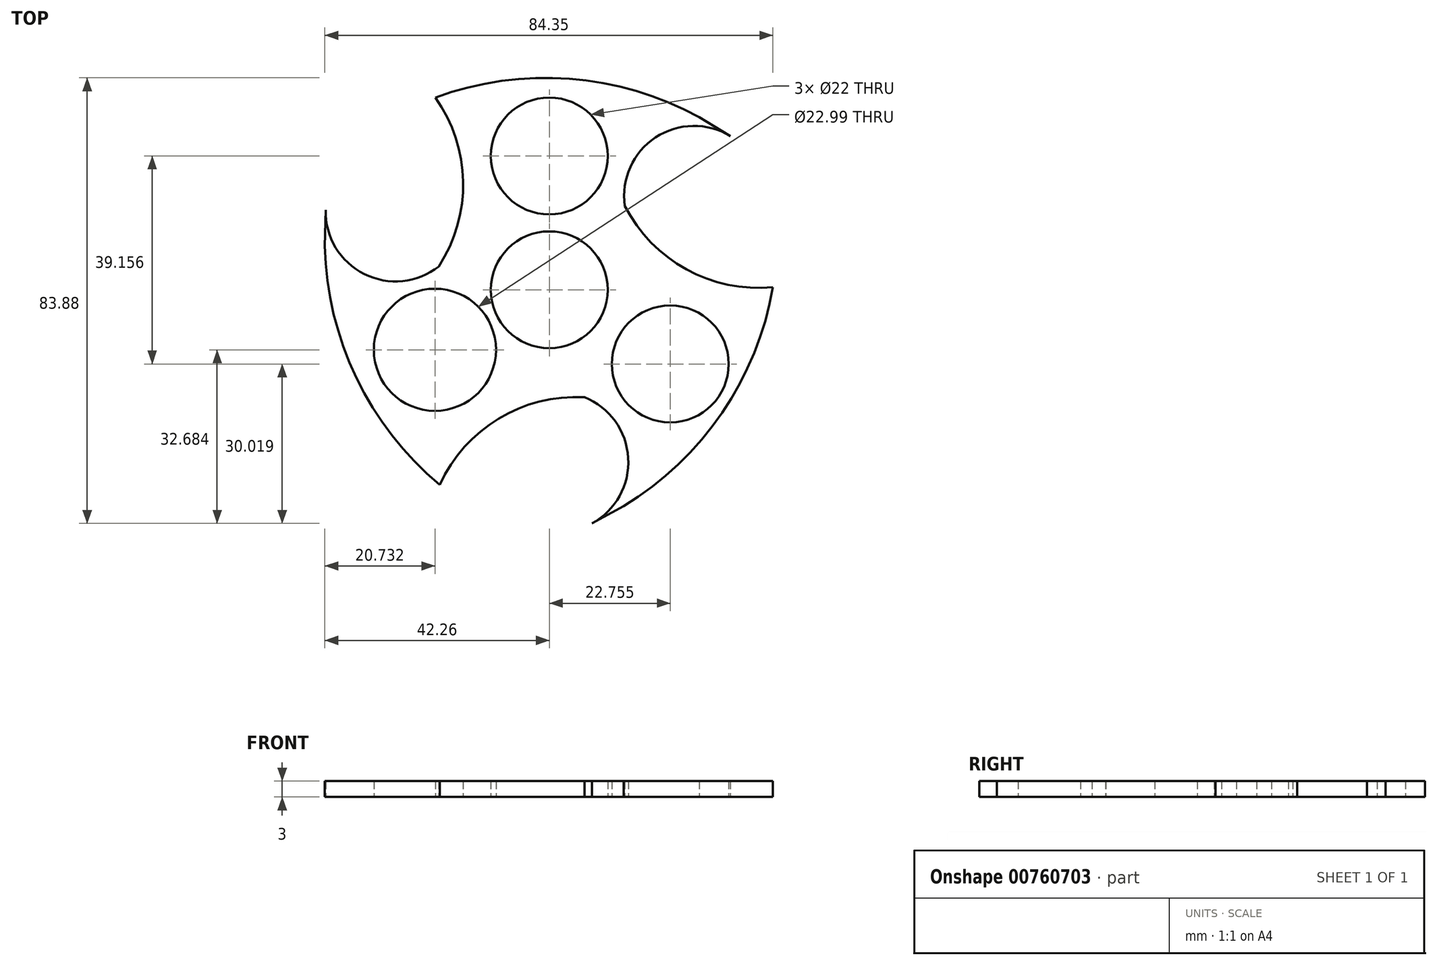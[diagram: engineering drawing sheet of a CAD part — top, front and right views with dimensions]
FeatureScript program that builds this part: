
annotation { "Feature Type Name" : "Feature", "Feature Type Description" : "" }
export const myFeature = defineFeature(function(context is Context, id is Id, definition is map)
    precondition{}
    {
        {
            var Q0;
            Q0=qCreatedBy(makeId("Top.planeOp"),FACE);
            var sketch = newSketch(context, id + "F0", { "sketchPlane" : qUnion([Q0])});
            skArc(sketch, "E0", {"start": v(28.24, 32.49) * mm, "mid": v(3.79, 39.73) * mm, "end": v(-21.47, 36.2) * mm});
            skArc(sketch, "E1", {"start": v(34.07, 28.95) * mm, "mid": v(19.98, 28.68) * mm, "end": v(14.21, 15.82) * mm});
            skArc(sketch, "E2", {"start": v(-20.8, 4.4) * mm, "mid": v(-16.22, 20.4) * mm, "end": v(-21.47, 36.2) * mm});
            skLineSegment(sketch, "E3", {"start": v(28.24, 32.49) * mm, "end": v(34.07, 28.95) * mm});
            skArc(sketch, "E4.1.5", {"start": v(9.53, 5.5) * mm, "mid": v(0, 11) * mm, "end": v(-9.53, 5.5) * mm});
            skArc(sketch, "E5.2.12", {"start": v(0, -11) * mm, "mid": v(9.53, -5.5) * mm, "end": v(9.53, 5.5) * mm});
            skCircle(sketch, "E6", {"center": v(0, 25.2) * mm, "radius": 11 * mm});
            skLineSegment(sketch, "E7.1.2", {"start": v(-42.26, 8.21) * mm, "end": v(-42.1, 15.04) * mm});
            skArc(sketch, "E7.1.4", {"start": v(6.6, -20.22) * mm, "mid": v(-9.56, -24.25) * mm, "end": v(-20.62, -36.7) * mm});
            skArc(sketch, "E7.1.5", {"start": v(-42.1, 15.04) * mm, "mid": v(-34.83, 2.97) * mm, "end": v(-20.8, 4.4) * mm});
            skCircle(sketch, "E7.1.6", {"center": v(-21.53, -11.3) * mm, "radius": 11.5 * mm});
            skArc(sketch, "E7.1.7", {"start": v(-42.26, 8.21) * mm, "mid": v(-36.3, -16.59) * mm, "end": v(-20.62, -36.7) * mm});
            skLineSegment(sketch, "E7.2.2", {"start": v(14.02, -40.7) * mm, "end": v(8.03, -43.98) * mm});
            skArc(sketch, "E7.2.3", {"start": v(-9.53, 5.5) * mm, "mid": v(-9.53, -5.5) * mm, "end": v(0, -11) * mm});
            skArc(sketch, "E7.2.4", {"start": v(14.21, 15.82) * mm, "mid": v(25.78, 3.85) * mm, "end": v(42.09, 0.49) * mm});
            skArc(sketch, "E7.2.5", {"start": v(8.03, -43.98) * mm, "mid": v(14.84, -31.65) * mm, "end": v(6.6, -20.22) * mm});
            skCircle(sketch, "E7.2.6", {"center": v(22.76, -13.96) * mm, "radius": 11 * mm});
            skArc(sketch, "E7.2.7", {"start": v(14.02, -40.7) * mm, "mid": v(32.51, -23.15) * mm, "end": v(42.09, 0.49) * mm});
            skSolve(sketch);
        }
        {
            var Q0;
            Q0 = qSketchRegion(id + "F0", true);
            extrude(context, id + "F1", {"entities" : qUnion([Q0]), "depth" : 3 * mm, "offsetDistance" : 25 * mm});
        }
    });
